# Revit family: РОСМА_ТермометрБиметаллическийСпец(Пружина)
name_source: partatom
category: Арматура трубопроводов
revit_build: Autodesk Revit 2018 (Build: 20180423_1000(x64)
units: mm (PartAtom-declared; Revit-internal decimal feet)

## family parameters
Всегда вертикально = Да
На основе рабочей плоскости = Нет
Общий = Нет
При загрузке вырезать с полостями = Нет
Размер круглого соединителя = Использовать диаметр
Тип детали = Клапан - Вставляется

## types (1)
- 30.010
    ADSK_Единица измерения = шт.
    ADSK_Количество = 1
    D = 63 мм
    D1 = 63 мм
    D2 = 62 мм
    Dполости_переднСт = 56 мм
    R1 шкала = 18 мм
    R2 шкала = 17 мм
    R_Logo = 10 мм
    Table1 = размеры_общетехнический специальный с пружиной
    Table2 = спец_общетехнический специальный с пружиной
    URL = https://rosma.spb.ru
    b = 13 мм
    b-e = 3 мм
    e = 10 мм
    Группа модели = Оборудование
    Диапазон раб. температур = от 0°С до +60°С
    Длина стрелки = 21 мм
    Изготовитель = ЗАО "РОСМА"
    Класс точности = 2,5
    Климатическое исполнение = Группа С2 по ГОСТ Р 52931; климатическое исполнение УХЛ категории 2.1 по ГОСТ 15150
    Код IP = IP43
    Описание = Тип БТ, серия 010. Термометр биметаллический накладной (термометр с пружиной) предназначен для измерения температуры поверхности трубы.
    Осевое присоединение = Да
    Присоединение = Стальная спиральная пружина для крепления на трубе диаметром от 20 до 50 мм
    Температура01 = ‎ : 0...+60°С
    Температура02 = ‎ : 0...+100°С
    Температура03 = ‎ : 0...+120°С
    Температура04 = ‎ : 0...+150°С
    Техническая документация = ТУ 4211-001-4719015564-2008
    лого_задн_стенка = Нет
